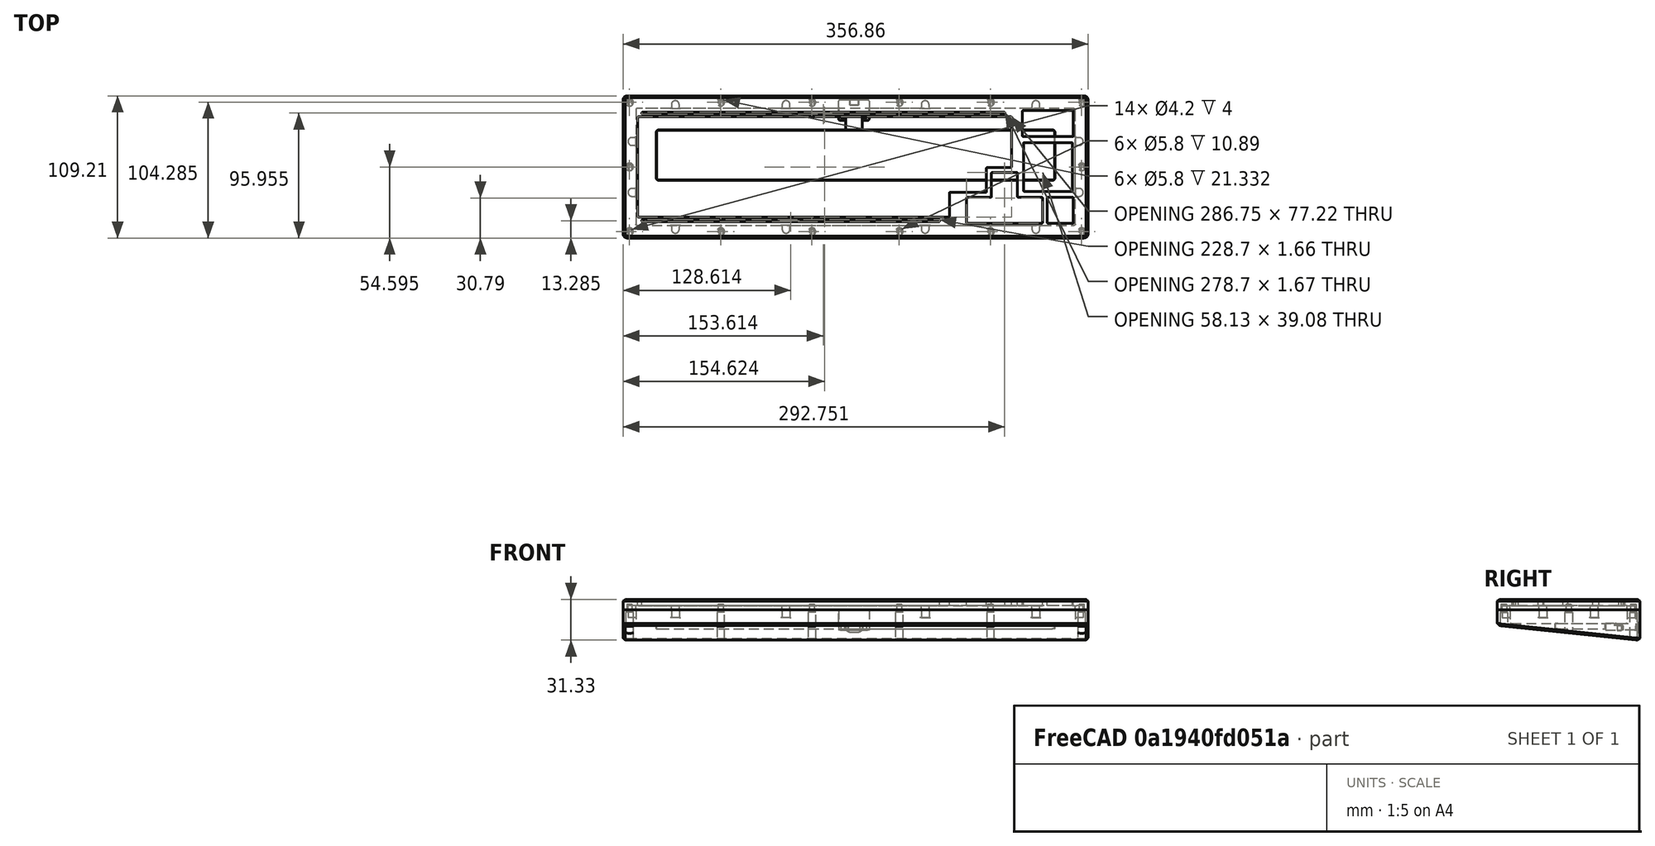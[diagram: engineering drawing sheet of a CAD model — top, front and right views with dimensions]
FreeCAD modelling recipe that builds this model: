
FCSTD DOCUMENT  (FreeCAD 1.0R39109 (Git))
Label: case
License: All rights reserved
LicenseURL: http://en.wikipedia.org/wiki/All_rights_reserved
objects: Part::Cylinder×58, Part::MultiFuse×51, Part::Feature×31, Part::Cut×14, Part::Extrusion×10, Part::Fillet×10, Part::Box×5, Part::Chamfer×2
note: 181 computed .brp shape members not serialized (recipe doc carries the construction recipe); baked Part::Feature solids carry a one-line shape summary decoded from their .brp

FEATURE [Part::Feature] path13_4_0_2_007
  shape: bbox 349.4 x 101.7 x 2e-07 mm, 0 faces, 0 solids (baked)
FEATURE [Part::Box] Box002  label="立方体002"
  AttacherType = Attacher::AttachEngine3D
  Height = 8
  Length = 356.862
  Placement = pos=(0,-109.21,0) rot=(0,0,1;0rad)
  Width = 109.21
FEATURE [Part::Extrusion] Extrude003
  Base = -> path13_4_0_2_007
  Dir = (0,0,1)
  DirMode = 0
  FaceMakerClass = Part::FaceMakerBullseye
  FaceMakerMode = 3
  LengthFwd = 3
  LengthRev = 0
  Solid = true
  Symmetric = false
FEATURE [Part::Cut] Cut004
  Base = -> Box002
  Tool = -> Extrude003
FEATURE [Part::Feature] path9
  shape: bbox 37.5 x 37.5 x 2e-07 mm, 0 faces, 0 solids (baked)
FEATURE [Part::Feature] path010
  shape: bbox 39.1 x 20.05 x 2e-07 mm, 0 faces, 0 solids (baked)
FEATURE [Part::Feature] path011
  shape: bbox 20.05 x 20.04 x 2e-07 mm, 0 faces, 0 solids (baked)
FEATURE [Part::Feature] path012
  shape: bbox 58.13 x 39.08 x 2e-07 mm, 0 faces, 0 solids (baked)
FEATURE [Part::Feature] path013
  shape: bbox 286.7 x 77.22 x 2e-07 mm, 0 faces, 0 solids (baked)
FEATURE [Part::MultiFuse] Fusion
  Shapes = -> [path9,path010,path011,path012,path013]
FEATURE [Part::Extrusion] Extrude004
  Base = -> Fusion
  Dir = (0,0,1)
  DirMode = 0
  FaceMakerClass = Part::FaceMakerBullseye
  FaceMakerMode = 3
  LengthFwd = 8
  LengthRev = 0
  Solid = true
  Symmetric = false
FEATURE [Part::Cut] Cut005
  Base = -> Cut004
  Tool = -> Extrude004
FEATURE [Part::Cylinder] Cylinder028  label="円柱028"
  Angle = 360
  AttacherType = Attacher::AttachEngine3D
  FirstAngle = 0
  Height = 30
  Placement = pos=(4.925,-4.925,-32) rot=(0,0,1;0rad)
  Radius = 2.9
  SecondAngle = 0
FEATURE [Part::Cylinder] Cylinder029  label="円柱029"
  Angle = 360
  AttacherType = Attacher::AttachEngine3D
  FirstAngle = 0
  Height = 30
  Placement = pos=(4.925,-54.6,-32) rot=(0,0,1;0rad)
  Radius = 2.9
  SecondAngle = 0
FEATURE [Part::Cylinder] Cylinder030  label="円柱030"
  Angle = 360
  AttacherType = Attacher::AttachEngine3D
  FirstAngle = 0
  Height = 30
  Placement = pos=(4.925,-104.28,-32) rot=(0,0,1;0rad)
  Radius = 2.9
  SecondAngle = 0
FEATURE [Part::Cylinder] Cylinder031  label="円柱031"
  Angle = 360
  AttacherType = Attacher::AttachEngine3D
  FirstAngle = 0
  Height = 30
  Placement = pos=(4.925,-4.925,-26) rot=(0,0,1;0rad)
  Radius = 2.1
  SecondAngle = 0
FEATURE [Part::Cylinder] Cylinder032  label="円柱032"
  Angle = 360
  AttacherType = Attacher::AttachEngine3D
  FirstAngle = 0
  Height = 30
  Placement = pos=(4.925,-104.28,-26) rot=(0,0,1;0rad)
  Radius = 2.1
  SecondAngle = 0
FEATURE [Part::Cylinder] Cylinder033  label="円柱033"
  Angle = 360
  AttacherType = Attacher::AttachEngine3D
  FirstAngle = 0
  Height = 30
  Placement = pos=(4.925,-54.6,-26) rot=(0,0,1;0rad)
  Radius = 2.1
  SecondAngle = 0
FEATURE [Part::Cylinder] Cylinder034  label="円柱034"
  Angle = 360
  AttacherType = Attacher::AttachEngine3D
  FirstAngle = 0
  Height = 30
  Placement = pos=(4.925,-4.925,-32) rot=(0,0,1;0rad)
  Radius = 2.9
  SecondAngle = 0
FEATURE [Part::Cylinder] Cylinder035  label="円柱035"
  Angle = 360
  AttacherType = Attacher::AttachEngine3D
  FirstAngle = 0
  Height = 30
  Placement = pos=(4.925,-104.28,-32) rot=(0,0,1;0rad)
  Radius = 2.9
  SecondAngle = 0
FEATURE [Part::Cylinder] Cylinder036  label="円柱036"
  Angle = 360
  AttacherType = Attacher::AttachEngine3D
  FirstAngle = 0
  Height = 30
  Placement = pos=(4.925,-4.925,-26) rot=(0,0,1;0rad)
  Radius = 2.1
  SecondAngle = 0
FEATURE [Part::Cylinder] Cylinder037  label="円柱037"
  Angle = 360
  AttacherType = Attacher::AttachEngine3D
  FirstAngle = 0
  Height = 30
  Placement = pos=(4.925,-104.28,-26) rot=(0,0,1;0rad)
  Radius = 2.1
  SecondAngle = 0
FEATURE [Part::Cylinder] Cylinder038  label="円柱038"
  Angle = 360
  AttacherType = Attacher::AttachEngine3D
  FirstAngle = 0
  Height = 30
  Placement = pos=(4.925,-4.925,-32) rot=(0,0,1;0rad)
  Radius = 2.9
  SecondAngle = 0
FEATURE [Part::Cylinder] Cylinder039  label="円柱039"
  Angle = 360
  AttacherType = Attacher::AttachEngine3D
  FirstAngle = 0
  Height = 30
  Placement = pos=(4.925,-104.28,-32) rot=(0,0,1;0rad)
  Radius = 2.9
  SecondAngle = 0
FEATURE [Part::Cylinder] Cylinder040  label="円柱040"
  Angle = 360
  AttacherType = Attacher::AttachEngine3D
  FirstAngle = 0
  Height = 30
  Placement = pos=(4.925,-4.925,-26) rot=(0,0,1;0rad)
  Radius = 2.1
  SecondAngle = 0
FEATURE [Part::Cylinder] Cylinder041  label="円柱041"
  Angle = 360
  AttacherType = Attacher::AttachEngine3D
  FirstAngle = 0
  Height = 30
  Placement = pos=(4.925,-104.28,-26) rot=(0,0,1;0rad)
  Radius = 2.1
  SecondAngle = 0
FEATURE [Part::Cylinder] Cylinder042  label="円柱042"
  Angle = 360
  AttacherType = Attacher::AttachEngine3D
  FirstAngle = 0
  Height = 30
  Placement = pos=(4.925,-4.925,-32) rot=(0,0,1;0rad)
  Radius = 2.9
  SecondAngle = 0
FEATURE [Part::Cylinder] Cylinder043  label="円柱043"
  Angle = 360
  AttacherType = Attacher::AttachEngine3D
  FirstAngle = 0
  Height = 30
  Placement = pos=(4.925,-54.6,-32) rot=(0,0,1;0rad)
  Radius = 2.9
  SecondAngle = 0
FEATURE [Part::Cylinder] Cylinder044  label="円柱044"
  Angle = 360
  AttacherType = Attacher::AttachEngine3D
  FirstAngle = 0
  Height = 30
  Placement = pos=(4.925,-104.28,-32) rot=(0,0,1;0rad)
  Radius = 2.9
  SecondAngle = 0
FEATURE [Part::Cylinder] Cylinder045  label="円柱045"
  Angle = 360
  AttacherType = Attacher::AttachEngine3D
  FirstAngle = 0
  Height = 30
  Placement = pos=(4.925,-4.925,-26) rot=(0,0,1;0rad)
  Radius = 2.1
  SecondAngle = 0
FEATURE [Part::Cylinder] Cylinder046  label="円柱046"
  Angle = 360
  AttacherType = Attacher::AttachEngine3D
  FirstAngle = 0
  Height = 30
  Placement = pos=(4.925,-104.28,-26) rot=(0,0,1;0rad)
  Radius = 2.1
  SecondAngle = 0
FEATURE [Part::Cylinder] Cylinder047  label="円柱047"
  Angle = 360
  AttacherType = Attacher::AttachEngine3D
  FirstAngle = 0
  Height = 30
  Placement = pos=(4.925,-54.6,-26) rot=(0,0,1;0rad)
  Radius = 2.1
  SecondAngle = 0
FEATURE [Part::Cylinder] Cylinder048  label="円柱048"
  Angle = 360
  AttacherType = Attacher::AttachEngine3D
  FirstAngle = 0
  Height = 30
  Placement = pos=(4.925,-4.925,-32) rot=(0,0,1;0rad)
  Radius = 2.9
  SecondAngle = 0
FEATURE [Part::Cylinder] Cylinder049  label="円柱049"
  Angle = 360
  AttacherType = Attacher::AttachEngine3D
  FirstAngle = 0
  Height = 30
  Placement = pos=(4.925,-104.28,-32) rot=(0,0,1;0rad)
  Radius = 2.9
  SecondAngle = 0
FEATURE [Part::Cylinder] Cylinder050  label="円柱050"
  Angle = 360
  AttacherType = Attacher::AttachEngine3D
  FirstAngle = 0
  Height = 30
  Placement = pos=(4.925,-4.925,-26) rot=(0,0,1;0rad)
  Radius = 2.1
  SecondAngle = 0
FEATURE [Part::Cylinder] Cylinder051  label="円柱051"
  Angle = 360
  AttacherType = Attacher::AttachEngine3D
  FirstAngle = 0
  Height = 30
  Placement = pos=(4.925,-104.28,-26) rot=(0,0,1;0rad)
  Radius = 2.1
  SecondAngle = 0
FEATURE [Part::Cylinder] Cylinder052  label="円柱052"
  Angle = 360
  AttacherType = Attacher::AttachEngine3D
  FirstAngle = 0
  Height = 30
  Placement = pos=(4.925,-4.925,-32) rot=(0,0,1;0rad)
  Radius = 2.9
  SecondAngle = 0
FEATURE [Part::Cylinder] Cylinder053  label="円柱053"
  Angle = 360
  AttacherType = Attacher::AttachEngine3D
  FirstAngle = 0
  Height = 30
  Placement = pos=(4.925,-104.28,-32) rot=(0,0,1;0rad)
  Radius = 2.9
  SecondAngle = 0
FEATURE [Part::Cylinder] Cylinder054  label="円柱054"
  Angle = 360
  AttacherType = Attacher::AttachEngine3D
  FirstAngle = 0
  Height = 30
  Placement = pos=(4.925,-4.925,-26) rot=(0,0,1;0rad)
  Radius = 2.1
  SecondAngle = 0
FEATURE [Part::Cylinder] Cylinder055  label="円柱055"
  Angle = 360
  AttacherType = Attacher::AttachEngine3D
  FirstAngle = 0
  Height = 30
  Placement = pos=(4.925,-104.28,-26) rot=(0,0,1;0rad)
  Radius = 2.1
  SecondAngle = 0
FEATURE [Part::MultiFuse] Fusion022
  Shapes = -> [Cylinder028,Cylinder031]
FEATURE [Part::MultiFuse] Fusion024
  Shapes = -> [Cylinder030,Cylinder032]
FEATURE [Part::MultiFuse] Fusion026
  Shapes = -> [Cylinder034,Cylinder036]
FEATURE [Part::MultiFuse] Fusion027
  Shapes = -> [Cylinder035,Cylinder037]
FEATURE [Part::MultiFuse] Fusion029
  Shapes = -> [Cylinder038,Cylinder040]
FEATURE [Part::MultiFuse] Fusion030
  Shapes = -> [Cylinder039,Cylinder041]
FEATURE [Part::MultiFuse] Fusion032
  Shapes = -> [Cylinder042,Cylinder045]
FEATURE [Part::MultiFuse] Fusion034
  Shapes = -> [Cylinder044,Cylinder046]
FEATURE [Part::MultiFuse] Fusion036
  Shapes = -> [Cylinder048,Cylinder050]
FEATURE [Part::MultiFuse] Fusion037
  Shapes = -> [Cylinder049,Cylinder051]
FEATURE [Part::MultiFuse] Fusion039
  Shapes = -> [Cylinder052,Cylinder054]
FEATURE [Part::MultiFuse] Fusion040
  Shapes = -> [Cylinder053,Cylinder055]
FEATURE [Part::MultiFuse] Fusion023
  Shapes = -> [Cylinder029,Cylinder033]
FEATURE [Part::MultiFuse] Fusion025
  Shapes = -> [Fusion022,Fusion024]
FEATURE [Part::MultiFuse] Fusion028
  Placement = pos=(70,0,0) rot=(0,0,1;0rad)
  Shapes = -> [Fusion026,Fusion027]
FEATURE [Part::MultiFuse] Fusion031
  Placement = pos=(140,0,0) rot=(0,0,1;0rad)
  Shapes = -> [Fusion029,Fusion030]
FEATURE [Part::MultiFuse] Fusion033
  Placement = pos=(347.01,0,0) rot=(0,0,1;0rad)
  Shapes = -> [Cylinder043,Cylinder047]
FEATURE [Part::MultiFuse] Fusion035
  Placement = pos=(347.01,0,0) rot=(0,0,1;0rad)
  Shapes = -> [Fusion032,Fusion034]
FEATURE [Part::MultiFuse] Fusion038
  Placement = pos=(207.01,0,0) rot=(0,0,1;0rad)
  Shapes = -> [Fusion036,Fusion037]
FEATURE [Part::MultiFuse] Fusion041
  Placement = pos=(277.01,0,0) rot=(0,0,1;0rad)
  Shapes = -> [Fusion039,Fusion040]
FEATURE [Part::MultiFuse] Fusion042
  Shapes = -> [Fusion023,Fusion025,Fusion028,Fusion031,Fusion033,Fusion035,Fusion038,Fusion041]
FEATURE [Part::Cut] Cut007
  Base = -> Cut005
  Tool = -> Fusion042
FEATURE [Part::Feature] rect1_1
  shape: bbox 278.7 x 1.665 x 2e-07 mm, 0 faces, 0 solids (baked)
FEATURE [Part::Feature] rect1_002
  shape: bbox 228.7 x 1.665 x 2e-07 mm, 0 faces, 0 solids (baked)
FEATURE [Part::MultiFuse] Fusion043
  Shapes = -> [rect1_1,rect1_002]
FEATURE [Part::Extrusion] Extrude005
  Base = -> Fusion043
  Dir = (0,0,1)
  DirMode = 0
  FaceMakerClass = Part::FaceMakerBullseye
  FaceMakerMode = 3
  LengthFwd = 5
  LengthRev = 0
  Solid = true
  Symmetric = false
FEATURE [Part::Fillet] Fillet
  Base = -> Extrude005
  EdgeLinks = -> Extrude005 [Edge1,Edge2,Edge5,Edge8,Edge13,Edge14,Edge17,Edge20]
  Edges = 8 edges r=0.8: [Edge1,Edge2,Edge5,Edge8,Edge13,Edge14,Edge17,Edge20]
  Placement = pos=(0,0,3) rot=(0,0,1;0rad)
FEATURE [Part::MultiFuse] Fusion044
  Shapes = -> [Cut007,Fillet]
FEATURE [Part::Fillet] Fillet001
  Base = -> Fusion044
  EdgeLinks = -> Fusion044 [Edge136,Edge137,Edge139,Edge141,Edge143,Edge145,Edge147,Edge149,Edge152,Edge153,Edge155,Edge157,Edge160,Edge161,Edge163,Edge165,Edge167,Edge169,Edge171,Edge173,Edge176,Edge177,Edge179,Edge181,Edge184,Edge185,Edge187,Edge189]
  Edges = 28 edges r=0.5: [Edge136,Edge137,Edge139,Edge141,Edge143,Edge145,Edge147,Edge149,Edge152,Edge153,Edge155,Edge157,Edge160,Edge161,Edge163,Edge165,Edge167,Edge169,Edge171,Edge173,Edge176,Edge177,Edge179,Edge181,Edge184,Edge185,Edge187,Edge189]
FEATURE [Part::Fillet] Fillet002
  Base = -> Fillet001
  EdgeLinks = -> Fillet001 [Edge355,Edge356,Edge357,Edge364,Edge365,Edge366,Edge367,Edge374,Edge375,Edge376,Edge377,Edge379,Edge384,Edge386,Edge387,Edge389,Edge394,Edge396,Edge397,Edge398,Edge399,Edge406,Edge407,Edge408,Edge409,Edge416,Edge417,Edge418]
  Edges = 28 edges r=1: [Edge355,Edge356,Edge357,Edge364,Edge365,Edge366,Edge367,Edge374,Edge375,Edge376,Edge377,Edge379,Edge384,Edge386,Edge387,Edge389,Edge394,Edge396,Edge397,Edge398,Edge399,Edge406,Edge407,Edge408,Edge409,Edge416,Edge417,Edge418]
FEATURE [Part::Fillet] Fillet003
  Base = -> Fillet002
  EdgeLinks = -> Fillet002 [Edge499,Edge500,Edge501,Edge502]
  Edges = 4 edges r=3: [Edge499,Edge500,Edge501,Edge502]
FEATURE [Part::Chamfer] Chamfer
  Base = -> Fillet003
  EdgeLinks = -> Fillet003 [Edge125]
  Edges = 1 edges r=1.5: [Edge125]
FEATURE [Part::Feature] rect1_003
  shape: bbox 228.7 x 1.665 x 2e-07 mm, 0 faces, 0 solids (baked)
FEATURE [Part::Feature] rect1_004
  shape: bbox 278.7 x 1.665 x 2e-07 mm, 0 faces, 0 solids (baked)
FEATURE [Part::MultiFuse] Fusion045
  Shapes = -> [rect1_004,rect1_003]
FEATURE [Part::Extrusion] Extrude006
  Base = -> Fusion045
  Dir = (0,0,1)
  DirMode = 0
  FaceMakerClass = Part::FaceMakerBullseye
  FaceMakerMode = 3
  LengthFwd = 5
  LengthRev = 0
  Solid = true
  Symmetric = false
FEATURE [Part::Fillet] Fillet004
  Base = -> Extrude006
  EdgeLinks = -> Extrude006 [Edge1,Edge2,Edge5,Edge8,Edge13,Edge14,Edge17,Edge20]
  Edges = 8 edges r=0.8: [Edge1,Edge2,Edge5,Edge8,Edge13,Edge14,Edge17,Edge20]
  Placement = pos=(0,0,3) rot=(0,0,1;0rad)
FEATURE [Part::Feature] rect1_005
  shape: bbox 228.7 x 1.665 x 2e-07 mm, 0 faces, 0 solids (baked)
FEATURE [Part::Feature] rect1_006
  shape: bbox 278.7 x 1.665 x 2e-07 mm, 0 faces, 0 solids (baked)
FEATURE [Part::MultiFuse] Fusion046
  Shapes = -> [rect1_006,rect1_005]
FEATURE [Part::Extrusion] Extrude007
  Base = -> Fusion046
  Dir = (0,0,1)
  DirMode = 0
  FaceMakerClass = Part::FaceMakerBullseye
  FaceMakerMode = 3
  LengthFwd = 5
  LengthRev = 0
  Solid = true
  Symmetric = false
FEATURE [Part::Fillet] Fillet005  label="led-diffuser"
  Base = -> Extrude007
  EdgeLinks = -> Extrude007 [Edge1,Edge2,Edge5,Edge8,Edge13,Edge14,Edge17,Edge20]
  Edges = 8 edges r=0.8: [Edge1,Edge2,Edge5,Edge8,Edge13,Edge14,Edge17,Edge20]
  Placement = pos=(0,0,3) rot=(0,0,1;0rad)
FEATURE [Part::Cut] Cut008  label="top-case"
  Base = -> Chamfer
  Tool = -> Fillet004
FEATURE [Part::Box] Box003  label="立方体003"
  AttacherType = Attacher::AttachEngine3D
  Height = 4.2
  Length = 305.5
  Placement = pos=(25.68,-64.7,-14.8) rot=(0,0,1;0rad)
  Width = 38.3
FEATURE [Part::Fillet] Fillet007  label="weight"
  Base = -> Box003
  EdgeLinks = -> Box003 [Edge1,Edge3,Edge5,Edge7]
  Edges = 4 edges r=2: [Edge1,Edge3,Edge5,Edge7]
FEATURE [Part::Box] Box007  label="立方体007"
  AttacherType = Attacher::AttachEngine3D
  Height = 4.3
  Length = 306
  Placement = pos=(25.43,-64.97,-14.8) rot=(0,0,1;0rad)
  Width = 38.8
FEATURE [Part::Cylinder] Cylinder058  label="円柱058"
  Angle = 360
  AttacherType = Attacher::AttachEngine3D
  FirstAngle = 0
  Height = 30
  Placement = pos=(4.925,-4.925,-32) rot=(0,0,1;0rad)
  Radius = 2.9
  SecondAngle = 0
FEATURE [Part::Cylinder] Cylinder059  label="円柱059"
  Angle = 360
  AttacherType = Attacher::AttachEngine3D
  FirstAngle = 0
  Height = 30
  Placement = pos=(4.925,-54.6,-32) rot=(0,0,1;0rad)
  Radius = 2.9
  SecondAngle = 0
FEATURE [Part::Cylinder] Cylinder060  label="円柱060"
  Angle = 360
  AttacherType = Attacher::AttachEngine3D
  FirstAngle = 0
  Height = 30
  Placement = pos=(4.925,-104.28,-32) rot=(0,0,1;0rad)
  Radius = 2.9
  SecondAngle = 0
FEATURE [Part::Cylinder] Cylinder061  label="円柱061"
  Angle = 360
  AttacherType = Attacher::AttachEngine3D
  FirstAngle = 0
  Height = 30
  Placement = pos=(4.925,-4.925,-30) rot=(0,0,1;0rad)
  Radius = 1.7
  SecondAngle = 0
FEATURE [Part::Cylinder] Cylinder062  label="円柱062"
  Angle = 360
  AttacherType = Attacher::AttachEngine3D
  FirstAngle = 0
  Height = 30
  Placement = pos=(4.925,-104.28,-30) rot=(0,0,1;0rad)
  Radius = 1.7
  SecondAngle = 0
FEATURE [Part::Cylinder] Cylinder063  label="円柱063"
  Angle = 360
  AttacherType = Attacher::AttachEngine3D
  FirstAngle = 0
  Height = 30
  Placement = pos=(4.925,-54.6,-30) rot=(0,0,1;0rad)
  Radius = 1.7
  SecondAngle = 0
FEATURE [Part::Cylinder] Cylinder064  label="円柱064"
  Angle = 360
  AttacherType = Attacher::AttachEngine3D
  FirstAngle = 0
  Height = 30
  Placement = pos=(4.925,-4.925,-32) rot=(0,0,1;0rad)
  Radius = 2.9
  SecondAngle = 0
FEATURE [Part::Cylinder] Cylinder065  label="円柱065"
  Angle = 360
  AttacherType = Attacher::AttachEngine3D
  FirstAngle = 0
  Height = 30
  Placement = pos=(4.925,-104.28,-32) rot=(0,0,1;0rad)
  Radius = 2.9
  SecondAngle = 0
FEATURE [Part::Cylinder] Cylinder066  label="円柱066"
  Angle = 360
  AttacherType = Attacher::AttachEngine3D
  FirstAngle = 0
  Height = 30
  Placement = pos=(4.925,-4.925,-30) rot=(0,0,1;0rad)
  Radius = 1.7
  SecondAngle = 0
FEATURE [Part::Cylinder] Cylinder067  label="円柱067"
  Angle = 360
  AttacherType = Attacher::AttachEngine3D
  FirstAngle = 0
  Height = 30
  Placement = pos=(4.925,-104.28,-30) rot=(0,0,1;0rad)
  Radius = 1.7
  SecondAngle = 0
FEATURE [Part::Cylinder] Cylinder068  label="円柱068"
  Angle = 360
  AttacherType = Attacher::AttachEngine3D
  FirstAngle = 0
  Height = 30
  Placement = pos=(4.925,-4.925,-32) rot=(0,0,1;0rad)
  Radius = 2.9
  SecondAngle = 0
FEATURE [Part::Cylinder] Cylinder069  label="円柱069"
  Angle = 360
  AttacherType = Attacher::AttachEngine3D
  FirstAngle = 0
  Height = 30
  Placement = pos=(4.925,-104.28,-32) rot=(0,0,1;0rad)
  Radius = 2.9
  SecondAngle = 0
FEATURE [Part::Cylinder] Cylinder070  label="円柱070"
  Angle = 360
  AttacherType = Attacher::AttachEngine3D
  FirstAngle = 0
  Height = 30
  Placement = pos=(4.925,-4.925,-30) rot=(0,0,1;0rad)
  Radius = 1.7
  SecondAngle = 0
FEATURE [Part::Cylinder] Cylinder071  label="円柱071"
  Angle = 360
  AttacherType = Attacher::AttachEngine3D
  FirstAngle = 0
  Height = 30
  Placement = pos=(4.925,-104.28,-30) rot=(0,0,1;0rad)
  Radius = 1.7
  SecondAngle = 0
FEATURE [Part::Cylinder] Cylinder072  label="円柱072"
  Angle = 360
  AttacherType = Attacher::AttachEngine3D
  FirstAngle = 0
  Height = 30
  Placement = pos=(4.925,-4.925,-32) rot=(0,0,1;0rad)
  Radius = 2.9
  SecondAngle = 0
FEATURE [Part::Cylinder] Cylinder073  label="円柱073"
  Angle = 360
  AttacherType = Attacher::AttachEngine3D
  FirstAngle = 0
  Height = 30
  Placement = pos=(4.925,-54.6,-32) rot=(0,0,1;0rad)
  Radius = 2.9
  SecondAngle = 0
FEATURE [Part::Cylinder] Cylinder074  label="円柱074"
  Angle = 360
  AttacherType = Attacher::AttachEngine3D
  FirstAngle = 0
  Height = 30
  Placement = pos=(4.925,-104.28,-32) rot=(0,0,1;0rad)
  Radius = 2.9
  SecondAngle = 0
FEATURE [Part::Cylinder] Cylinder075  label="円柱075"
  Angle = 360
  AttacherType = Attacher::AttachEngine3D
  FirstAngle = 0
  Height = 30
  Placement = pos=(4.925,-4.925,-30) rot=(0,0,1;0rad)
  Radius = 1.7
  SecondAngle = 0
FEATURE [Part::Cylinder] Cylinder076  label="円柱076"
  Angle = 360
  AttacherType = Attacher::AttachEngine3D
  FirstAngle = 0
  Height = 30
  Placement = pos=(4.925,-104.28,-30) rot=(0,0,1;0rad)
  Radius = 1.7
  SecondAngle = 0
FEATURE [Part::Cylinder] Cylinder077  label="円柱077"
  Angle = 360
  AttacherType = Attacher::AttachEngine3D
  FirstAngle = 0
  Height = 30
  Placement = pos=(4.925,-54.6,-30) rot=(0,0,1;0rad)
  Radius = 1.7
  SecondAngle = 0
FEATURE [Part::Cylinder] Cylinder078  label="円柱078"
  Angle = 360
  AttacherType = Attacher::AttachEngine3D
  FirstAngle = 0
  Height = 30
  Placement = pos=(4.925,-4.925,-32) rot=(0,0,1;0rad)
  Radius = 2.9
  SecondAngle = 0
FEATURE [Part::Cylinder] Cylinder079  label="円柱079"
  Angle = 360
  AttacherType = Attacher::AttachEngine3D
  FirstAngle = 0
  Height = 30
  Placement = pos=(4.925,-104.28,-32) rot=(0,0,1;0rad)
  Radius = 2.9
  SecondAngle = 0
FEATURE [Part::Cylinder] Cylinder080  label="円柱080"
  Angle = 360
  AttacherType = Attacher::AttachEngine3D
  FirstAngle = 0
  Height = 30
  Placement = pos=(4.925,-4.925,-30) rot=(0,0,1;0rad)
  Radius = 1.7
  SecondAngle = 0
FEATURE [Part::Cylinder] Cylinder081  label="円柱081"
  Angle = 360
  AttacherType = Attacher::AttachEngine3D
  FirstAngle = 0
  Height = 30
  Placement = pos=(4.925,-104.28,-30) rot=(0,0,1;0rad)
  Radius = 1.7
  SecondAngle = 0
FEATURE [Part::Cylinder] Cylinder082  label="円柱082"
  Angle = 360
  AttacherType = Attacher::AttachEngine3D
  FirstAngle = 0
  Height = 30
  Placement = pos=(4.925,-4.925,-32) rot=(0,0,1;0rad)
  Radius = 2.9
  SecondAngle = 0
FEATURE [Part::Cylinder] Cylinder083  label="円柱083"
  Angle = 360
  AttacherType = Attacher::AttachEngine3D
  FirstAngle = 0
  Height = 30
  Placement = pos=(4.925,-104.28,-32) rot=(0,0,1;0rad)
  Radius = 2.9
  SecondAngle = 0
FEATURE [Part::Cylinder] Cylinder084  label="円柱084"
  Angle = 360
  AttacherType = Attacher::AttachEngine3D
  FirstAngle = 0
  Height = 30
  Placement = pos=(4.925,-4.925,-30) rot=(0,0,1;0rad)
  Radius = 1.7
  SecondAngle = 0
FEATURE [Part::Cylinder] Cylinder085  label="円柱085"
  Angle = 360
  AttacherType = Attacher::AttachEngine3D
  FirstAngle = 0
  Height = 30
  Placement = pos=(4.925,-104.28,-30) rot=(0,0,1;0rad)
  Radius = 1.7
  SecondAngle = 0
FEATURE [Part::Cylinder] Cylinder086  label="円柱086"
  Angle = 360
  AttacherType = Attacher::AttachEngine3D
  FirstAngle = 0
  Height = 4
  Placement = pos=(168.72,-15.73,-16) rot=(0,0,1;0rad)
  Radius = 1.6
  SecondAngle = 0
FEATURE [Part::Cylinder] Cylinder087  label="円柱087"
  Angle = 360
  AttacherType = Attacher::AttachEngine3D
  FirstAngle = 0
  Height = 4
  Placement = pos=(185.53,-15.73,-16) rot=(0,0,1;0rad)
  Radius = 1.6
  SecondAngle = 0
FEATURE [Part::Fillet] Fillet009
  Base = -> Box007
  EdgeLinks = -> Box007 [Edge1,Edge3,Edge5,Edge7]
  Edges = 4 edges r=2: [Edge1,Edge3,Edge5,Edge7]
FEATURE [Part::MultiFuse] Fusion068
  Shapes = -> [Cylinder058,Cylinder061]
FEATURE [Part::MultiFuse] Fusion069
  Shapes = -> [Cylinder059,Cylinder063]
FEATURE [Part::MultiFuse] Fusion070
  Shapes = -> [Cylinder060,Cylinder062]
FEATURE [Part::MultiFuse] Fusion071
  Shapes = -> [Fusion068,Fusion070]
FEATURE [Part::MultiFuse] Fusion072
  Shapes = -> [Cylinder064,Cylinder066]
FEATURE [Part::MultiFuse] Fusion073
  Shapes = -> [Cylinder065,Cylinder067]
FEATURE [Part::MultiFuse] Fusion074
  Placement = pos=(70,0,0) rot=(0,0,1;0rad)
  Shapes = -> [Fusion072,Fusion073]
FEATURE [Part::MultiFuse] Fusion075
  Shapes = -> [Cylinder068,Cylinder070]
FEATURE [Part::MultiFuse] Fusion076
  Shapes = -> [Cylinder069,Cylinder071]
FEATURE [Part::MultiFuse] Fusion077
  Placement = pos=(140,0,0) rot=(0,0,1;0rad)
  Shapes = -> [Fusion075,Fusion076]
FEATURE [Part::MultiFuse] Fusion078
  Shapes = -> [Cylinder072,Cylinder075]
FEATURE [Part::MultiFuse] Fusion079
  Placement = pos=(347.01,0,0) rot=(0,0,1;0rad)
  Shapes = -> [Cylinder073,Cylinder077]
FEATURE [Part::MultiFuse] Fusion080
  Shapes = -> [Cylinder074,Cylinder076]
FEATURE [Part::MultiFuse] Fusion081
  Placement = pos=(347.01,0,0) rot=(0,0,1;0rad)
  Shapes = -> [Fusion078,Fusion080]
FEATURE [Part::MultiFuse] Fusion082
  Shapes = -> [Cylinder078,Cylinder080]
FEATURE [Part::MultiFuse] Fusion083
  Shapes = -> [Cylinder079,Cylinder081]
FEATURE [Part::MultiFuse] Fusion084
  Placement = pos=(207.01,0,0) rot=(0,0,1;0rad)
  Shapes = -> [Fusion082,Fusion083]
FEATURE [Part::MultiFuse] Fusion085
  Shapes = -> [Cylinder082,Cylinder084]
FEATURE [Part::MultiFuse] Fusion086
  Shapes = -> [Cylinder083,Cylinder085]
FEATURE [Part::MultiFuse] Fusion087
  Placement = pos=(277.01,0,0) rot=(0,0,1;0rad)
  Shapes = -> [Fusion085,Fusion086]
FEATURE [Part::MultiFuse] Fusion088
  Shapes = -> [Fusion087,Fusion069,Fusion071,Fusion074,Fusion077,Fusion079,Fusion081,Fusion084]
FEATURE [Part::MultiFuse] Fusion089
  Shapes = -> [Cylinder086,Cylinder087]
FEATURE [Part::Feature] hull008
  Placement = pos=(0,4.8,0) rot=(0,0,1;0rad)
  shape: bbox 13.02 x 10 x 7.518 mm, 128 faces (baked)
FEATURE [Part::Feature] hull009
  shape: bbox 9.26 x 10 x 3.733 mm, 28 faces (baked)
FEATURE [Part::Feature] rect002
  shape: bbox 23.2 x 16.03 x 2e-07 mm, 0 faces, 0 solids (baked)
FEATURE [Part::Extrusion] Extrude012
  Base = -> rect002
  Dir = (0,0,-1)
  DirMode = 0
  FaceMakerClass = Part::FaceMakerBullseye
  FaceMakerMode = 3
  LengthFwd = 12.1
  LengthRev = 0
  Solid = true
  Symmetric = false
FEATURE [Part::Feature] rect1_0_010
  Placement = pos=(0,0,-10.5) rot=(0,0,1;0rad)
  shape: bbox 12.63 x 23.28 x 2e-07 mm, 0 faces, 0 solids (baked)
FEATURE [Part::Extrusion] Extrude013
  Base = -> rect1_0_010
  Dir = (0,0,-1)
  DirMode = 0
  FaceMakerClass = Part::FaceMakerBullseye
  FaceMakerMode = 3
  LengthFwd = 5.1
  LengthRev = 0
  Solid = true
  Symmetric = false
FEATURE [Part::Box] Box008  label="立方体008"
  AttacherType = Attacher::AttachEngine3D
  Height = 40
  Length = 356.862
  Placement = pos=(0,-109.21,-40) rot=(0,0,1;0rad)
  Width = 109.21
FEATURE [Part::Box] Box009  label="立方体009"
  AttacherType = Attacher::AttachEngine3D
  Height = 100
  Length = 356.862
  Placement = pos=(0,-120.21,-111.4) rot=(1,0,0;-0.10472rad)
  Width = 159.21
FEATURE [Part::Feature] path13_4_0_2_010
  shape: bbox 337.4 x 89.71 x 2e-07 mm, 0 faces, 0 solids (baked)
FEATURE [Part::Extrusion] Extrude014
  Base = -> path13_4_0_2_010
  Dir = (0,0,-1)
  DirMode = 0
  FaceMakerClass = Part::FaceMakerBullseye
  FaceMakerMode = 3
  LengthFwd = 10.5
  LengthRev = 0
  Solid = true
  Symmetric = false
FEATURE [Part::Feature] path13_4_0_2_011 .. path13_4_0_2_022  x12 (patterned run collapsed; names and placements below)
  shape: bbox 6 x 6 x 2e-07 mm, 0 faces, 0 solids (baked)
FEATURE [Part::MultiFuse] Fusion091
  Shapes = -> [path13_4_0_2_011,path13_4_0_2_012,path13_4_0_2_013,path13_4_0_2_014,path13_4_0_2_015,path13_4_0_2_016,path13_4_0_2_017,path13_4_0_2_018,path13_4_0_2_019,path13_4_0_2_020,path13_4_0_2_021,path13_4_0_2_022]
FEATURE [Part::Cut] Cut022
  Base = -> Box008
  Tool = -> Box009
FEATURE [Part::Cut] Cut023
  Base = -> Cut022
  Tool = -> Extrude014
FEATURE [Part::Extrusion] Extrude015
  Base = -> Fusion091
  Dir = (0,0,-1)
  DirMode = 0
  FaceMakerClass = Part::FaceMakerBullseye
  FaceMakerMode = 3
  LengthFwd = 6.2
  LengthRev = 0
  Solid = true
  Symmetric = false
FEATURE [Part::Cut] Cut024
  Base = -> Cut023
  Tool = -> Extrude015
FEATURE [Part::Cut] Cut025
  Base = -> Cut024
  Tool = -> Extrude012
FEATURE [Part::Cut] Cut026
  Base = -> Cut025
  Tool = -> Extrude013
FEATURE [Part::Cut] Cut027
  Base = -> Cut026
  Tool = -> Fillet009
FEATURE [Part::MultiFuse] Fusion090  label="usb-hole001"
  Placement = pos=(-138.5,-4.3,-16.16) rot=(0,0,1;0rad)
  Shapes = -> [hull008,hull009]
FEATURE [Part::Cut] Cut028
  Base = -> Cut027
  Tool = -> Fusion090
FEATURE [Part::Cut] Cut029
  Base = -> Cut028
  Tool = -> Fusion089
FEATURE [Part::Cut] Cut030
  Base = -> Cut029
  Tool = -> Fusion088
FEATURE [Part::Feature] hull
  Placement = pos=(177.35,3,-13.68) rot=(1,0,0;1.5708rad)
  shape: bbox 9.4 x 10 x 3.971 mm, 28 faces (baked)
FEATURE [Part::Feature] rect1
  shape: bbox 23.2 x 10.03 x 2e-07 mm, 0 faces, 0 solids (baked)
FEATURE [Part::Extrusion] Extrude
  Base = -> rect1
  Dir = (0,0,-1)
  DirMode = 0
  FaceMakerClass = Part::FaceMakerBullseye
  FaceMakerMode = 3
  LengthFwd = 15.6
  LengthRev = 0
  Solid = true
  Symmetric = false
FEATURE [Part::MultiFuse] Fusion092
  Shapes = -> [hull,Extrude]
FEATURE [Part::Cut] Cut
  Base = -> Cut030
  Tool = -> Fusion092
FEATURE [Part::Fillet] Fillet010
  Base = -> Cut
  EdgeLinks = -> Cut [Edge1,Edge3,Edge6,Edge93]
  Edges = 4 edges r=3: [Edge1,Edge3,Edge6,Edge93]
FEATURE [Part::Chamfer] Chamfer001
  Base = -> Fillet010
  EdgeLinks = -> Fillet010 [Edge99]
  Edges = 1 edges r=1.5: [Edge99]
FEATURE [Part::Fillet] Fillet011  label="bottom-case"
  Base = -> Chamfer001
  EdgeLinks = -> Chamfer001 [Edge281,Edge283,Edge284,Edge286,Edge289,Edge290,Edge292,Edge293,Edge295,Edge297,Edge329,Edge330,Edge332,Edge333,Edge335,Edge336,Edge338,Edge339,Edge341,Edge343,Edge349,Edge352,Edge358,Edge360,Edge361,Edge363,Edge364,Edge396,Edge398,Edge399,Edge401,Edge730,Edge734,Edge746,Edge750,Edge778,Edge780,Edge803,Edge806]
  Edges = 39 edges r=1: [Edge281,Edge283,Edge284,Edge286,Edge289,Edge290,Edge292,Edge293,Edge295,Edge297,Edge329,Edge330,Edge332,Edge333,Edge335,Edge336,Edge338,Edge339,Edge341,Edge343,Edge349,Edge352,Edge358,Edge360,Edge361,Edge363,Edge364,Edge396,Edge398,Edge399,Edge401,Edge730,Edge734,Edge746,Edge750,Edge778,Edge780,+2 more]
